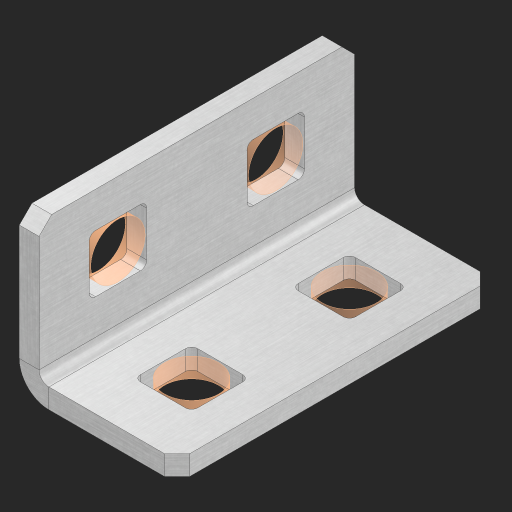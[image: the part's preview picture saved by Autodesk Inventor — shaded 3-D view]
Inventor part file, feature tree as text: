
AUTODESK INVENTOR PART (.ipt)
format: ipt  version: 2023 (Build 270158000, 158)  size: 486,912 bytes
history: native  units: in
note: dims shown in document units (in); Inventor stores cm internally (conversion verified against a paired STEP export)
features: other x10, sheet_metal_op x8, sketch x5, extrude x5, pattern_linear x1, mirror x1, chamfer x1
ambient origin geometry x8: Origin, YZ Plane, XZ Plane, XY Plane, X Axis, Y Axis, Z Axis, Center Point
bodies: Solid1 (feature_tree), Body (feature_tree)
feature tree (31):
  sheet_metal_op  "Flanges"
  sheet_metal_op  "Body Pattern"
  other  "Arc Length"
  pattern_linear  "Notch Pattern"  Spacing1=0.125in  [1 undecoded]
  other  "Diagonal Plane"
  mirror  "Everything Mirrored"
  chamfer  "End Chamfer"
  sketch  "Sketch1"  dims[d0=0.5in]
  other  "Plate1"
  sketch  "Sketch2"  dims[d1=1.0in]
  other  "Plate2"
  sheet_metal_op  "Bend1"
  sheet_metal_op  "Corner1"
  sketch  "Sketch8"  dims[d2=0.0625in]
  sketch  "Sketch9"  dims[d3=0.0625in]
  other  "Srf91"
  sheet_metal_op  "Body Pattern Sketch"
  other  "Srf92"
  sketch  "Sketch13"  dims[d4=0.0312in d5=0.125in d6=0.0625in d7=0.5in d8=90.0deg d9=0.0312in d10=0.25in d11=0.0625in d12=0.0625in d49=0.182in d50=0.02in d52=0.25in d53=0.0625in d54=0.0in d55=0.172in d56=1.0in d57=0.0in d85=0.1473in d86=0.1782in d89=0.0625in d90=0.0in d91=0.04in d92=0.0491in d95=2.5in d96=0.04in d97=0.25in d98=45.0deg d123=0.204in d126=0.0491in d127=0.1473in d128=0.08in d129=0.04in d130=2.5in d131=0.7874in d133=0.5in d134=0.3937in d136=1.0in]
  other  "Srf856"
  other  "Srf1275"
  other  "Srf1276"
  other  "Srf1278"
  sheet_metal_op  "Body Stamp"
  sheet_metal_op  "Body Circle"
  sheet_metal_op  "Notch"
  extrude  "ExtrusionSrf92"  Depth=0.0625in
  extrude  "ExtrusionSrf856"  Depth=0.5in TaperAngle=90.0deg
  extrude  "ExtrusionSrf1275"  Depth=0.25in
  extrude  "ExtrusionSrf1276"  Depth=0.0625in
  extrude  "ExtrusionSrf1277"  Depth=0.0625in
note: 1 required parameter value undecoded (feature->parameter linkage not recoverable at this tier; creation-order binding heuristic only, values carry confidence <= 0.55)
